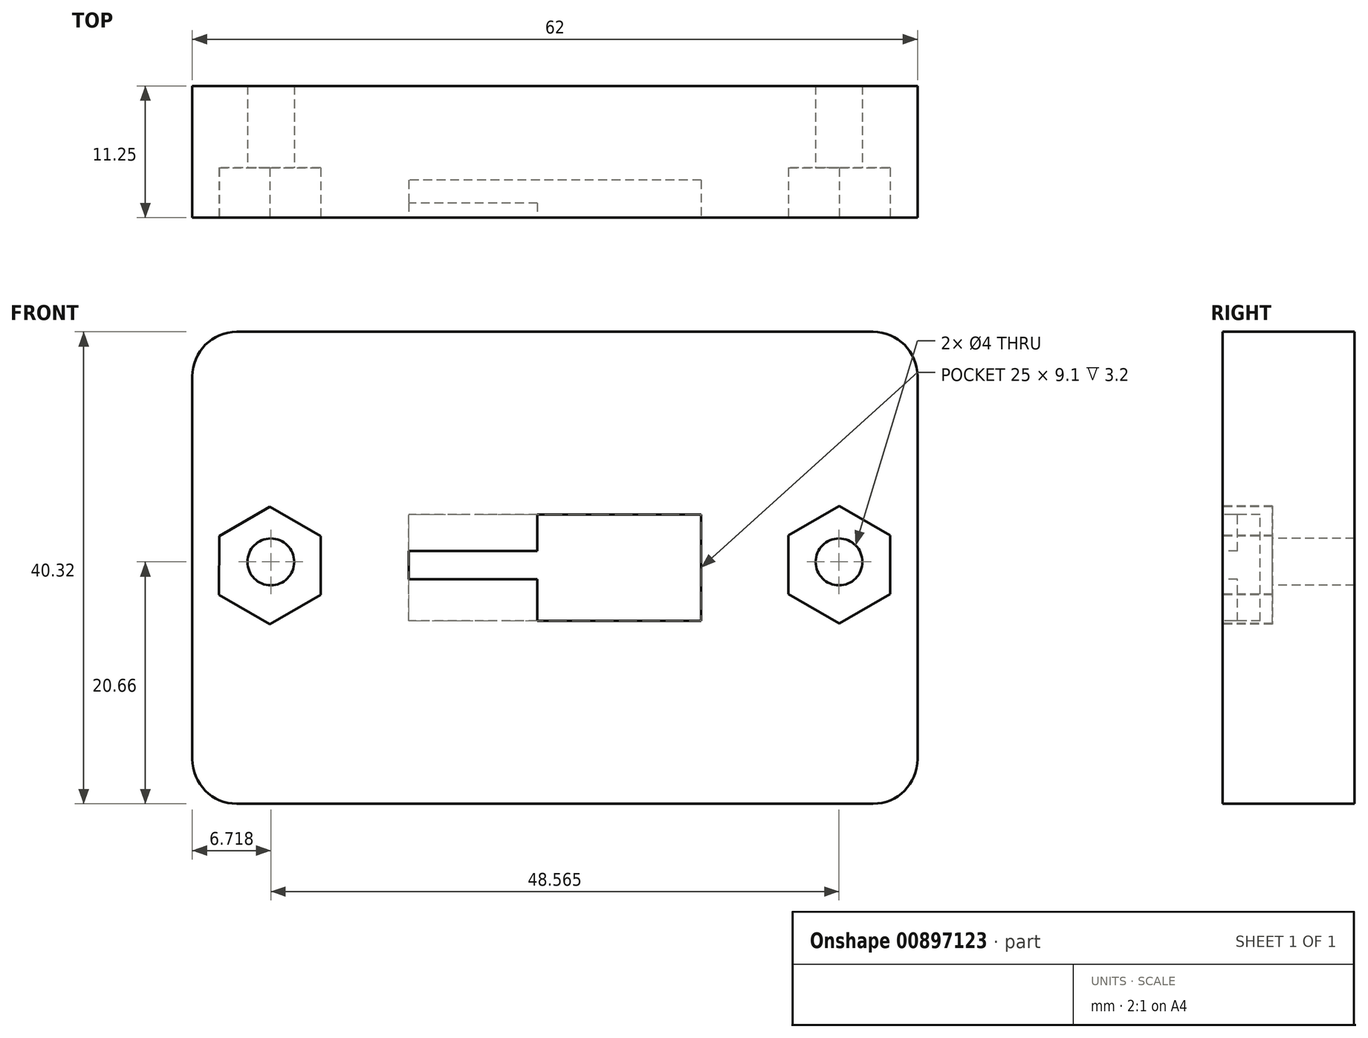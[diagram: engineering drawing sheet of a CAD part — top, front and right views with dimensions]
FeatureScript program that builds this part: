
annotation { "Feature Type Name" : "Feature", "Feature Type Description" : "" }
export const myFeature = defineFeature(function(context is Context, id is Id, definition is map)
    precondition{}
    {
        {
            var Q0;
            Q0=qCreatedBy(makeId("Front.planeOp"),FACE);
            var sketch = newSketch(context, id + "F0", { "sketchPlane" : qUnion([Q0])});
            skLineSegment(sketch, "E0.bottom", {"start": v(31, -20.16) * mm, "end": v(-31, -20.16) * mm});
            skLineSegment(sketch, "E0.top", {"start": v(31, 20.16) * mm, "end": v(-31, 20.16) * mm});
            skLineSegment(sketch, "E0.left", {"start": v(31, -20.16) * mm, "end": v(31, 20.16) * mm});
            skLineSegment(sketch, "E0.right", {"start": v(-31, -20.16) * mm, "end": v(-31, 20.16) * mm});
            skPoint(sketch, "E0.middle", {"position": v(0, 0) * mm});
            skSolve(sketch);
        }
        {
            var Q0;
            Q0=qSketchRegion(id+"F0",true);
            extrude(context, id + "F1", {"entities" : qUnion([Q0]), "depth" : 11.25 * mm, "offsetDistance" : 25.4 * mm});
        }
        {
            var Q0;
            Q0=makeQuery(id+"F1.opExtrude","CAP_FACE",FACE,{"disambiguationData":[OSD([sQuery(id+"F0.wireOp",EDGE,"E0.bottom"),sQuery(id+"F0.wireOp",EDGE,"E0.top"),sQuery(id+"F0.wireOp",EDGE,"E0.left"),sQuery(id+"F0.wireOp",EDGE,"E0.right")])],"isStart":false});
            var sketch = newSketch(context, id + "F2", { "sketchPlane" : qUnion([Q0])});
            skLineSegment(sketch, "E1.bottom", {"start": v(12.5, -4.55) * mm, "end": v(-12.5, -4.55) * mm});
            skLineSegment(sketch, "E1.top", {"start": v(12.5, 4.55) * mm, "end": v(-12.5, 4.55) * mm});
            skLineSegment(sketch, "E1.left", {"start": v(12.5, -4.55) * mm, "end": v(12.5, 4.55) * mm});
            skLineSegment(sketch, "E1.right", {"start": v(-12.5, -4.55) * mm, "end": v(-12.5, 4.55) * mm});
            skPoint(sketch, "E1.middle", {"position": v(0, 0) * mm});
            skSolve(sketch);
        }
        {
            var Q0;
            Q0=qSketchRegion(id+"F2",true);
            extrude(context, id + "F3", {"entities" : qUnion([Q0]), "operationType" : NewBodyOperationType.REMOVE, "oppositeDirection" : true, "depth" : 3.2 * mm, "offsetDistance" : 25.4 * mm});
        }
        {
            var Q0;
            Q0=makeQuery(id+"F1.opExtrude","CAP_FACE",FACE,{"disambiguationData":[OSD([sQuery(id+"F0.wireOp",EDGE,"E0.bottom"),sQuery(id+"F0.wireOp",EDGE,"E0.top"),sQuery(id+"F0.wireOp",EDGE,"E0.left"),sQuery(id+"F0.wireOp",EDGE,"E0.right")])],"isStart":false});
            var sketch = newSketch(context, id + "F4", { "sketchPlane" : qUnion([Q0])});
            skLineSegment(sketch, "E2.bottom", {"start": v(-12.5, 4.55) * mm, "end": v(-1.5, 4.55) * mm});
            skLineSegment(sketch, "E2.top", {"start": v(-12.5, 1.44) * mm, "end": v(-1.5, 1.44) * mm});
            skLineSegment(sketch, "E2.left", {"start": v(-12.5, 4.55) * mm, "end": v(-12.5, 1.44) * mm});
            skLineSegment(sketch, "E2.right", {"start": v(-1.5, 4.55) * mm, "end": v(-1.5, 1.44) * mm});
            skLineSegment(sketch, "E3.bottom", {"start": v(-12.5, -0.96) * mm, "end": v(-1.5, -0.96) * mm});
            skLineSegment(sketch, "E3.top", {"start": v(-12.5, -4.55) * mm, "end": v(-1.5, -4.55) * mm});
            skLineSegment(sketch, "E3.left", {"start": v(-12.5, -0.96) * mm, "end": v(-12.5, -4.55) * mm});
            skLineSegment(sketch, "E3.right", {"start": v(-1.5, -0.96) * mm, "end": v(-1.5, -4.55) * mm});
            skLineSegment(sketch, "E4.left", {"start": v(-12.5, 1.44) * mm, "end": v(-12.5, -0.96) * mm});
            skLineSegment(sketch, "E4.right", {"start": v(-1.5, 1.44) * mm, "end": v(-1.5, -0.96) * mm});
            skSolve(sketch);
        }
        {
            var Q0;
            Q0=makeQuery(id+"F4.imprint","IMPRINT",FACE,{"disambiguationData":[TD([[makeQuery(id+"F4.imprint","IMPRINT",EDGE,{"derivedFrom":sQuery(id+"F4.wireOp",EDGE,"E2.bottom")}),1.0]])]});
            var Q1;
            Q1=makeQuery(id+"F4.imprint","IMPRINT",FACE,{"disambiguationData":[TD([[makeQuery(id+"F4.imprint","IMPRINT",EDGE,{"derivedFrom":sQuery(id+"F4.wireOp",EDGE,"E3.top")}),-1.0]])]});
            extrude(context, id + "F5", {"entities" : qUnion([Q0, Q1]), "operationType" : NewBodyOperationType.ADD, "oppositeDirection" : true, "depth" : 1.25 * mm, "offsetDistance" : 25.4 * mm});
        }
        {
            var Q0;
            Q0=makeQuery(id+"F1.opExtrude","SWEPT_EDGE",EDGE,{"disambiguationData":[OSD([sQuery(id+"F0.wireOp",EDGE,"E0.top"),sQuery(id+"F0.wireOp",EDGE,"E0.right")])]});
            var Q1;
            Q1=makeQuery(id+"F1.opExtrude","SWEPT_EDGE",EDGE,{"disambiguationData":[OSD([sQuery(id+"F0.wireOp",EDGE,"E0.top"),sQuery(id+"F0.wireOp",EDGE,"E0.left")])]});
            var Q2;
            Q2=makeQuery(id+"F1.opExtrude","SWEPT_EDGE",EDGE,{"disambiguationData":[OSD([sQuery(id+"F0.wireOp",EDGE,"E0.bottom"),sQuery(id+"F0.wireOp",EDGE,"E0.left")])]});
            var Q3;
            Q3=makeQuery(id+"F1.opExtrude","SWEPT_EDGE",EDGE,{"disambiguationData":[OSD([sQuery(id+"F0.wireOp",EDGE,"E0.bottom"),sQuery(id+"F0.wireOp",EDGE,"E0.right")])]});
            fillet(context, id + "F6", {"entities" : qUnion([Q0, Q1, Q2, Q3]), "radius" : 3.8 * mm, "tangentPropagation" : true, "allowEdgeOverflow" : false});
        }
        {
            var Q0;
            Q0=makeQuery(id+"F5.boolean.opBoolean","MERGE",FACE,{"derivedFrom":[makeQuery(id+"F1.opExtrude","CAP_FACE",FACE,{"disambiguationData":[OSD([sQuery(id+"F0.wireOp",EDGE,"E0.bottom"),sQuery(id+"F0.wireOp",EDGE,"E0.top"),sQuery(id+"F0.wireOp",EDGE,"E0.left"),sQuery(id+"F0.wireOp",EDGE,"E0.right")])],"isStart":false}),makeQuery(id+"F5.opExtrude","CAP_FACE",FACE,{"disambiguationData":[OSD([sQuery(id+"F4.wireOp",EDGE,"E2.bottom"),sQuery(id+"F4.wireOp",EDGE,"E2.left"),sQuery(id+"F4.wireOp",EDGE,"E2.right"),sQuery(id+"F4.wireOp",EDGE,"E2.top")])],"isStart":true}),makeQuery(id+"F5.opExtrude","CAP_FACE",FACE,{"disambiguationData":[OSD([sQuery(id+"F4.wireOp",EDGE,"E3.top"),sQuery(id+"F4.wireOp",EDGE,"E3.left"),sQuery(id+"F4.wireOp",EDGE,"E3.right"),sQuery(id+"F4.wireOp",EDGE,"E3.bottom")])],"isStart":true})]});
            var sketch = newSketch(context, id + "F7", { "sketchPlane" : qUnion([Q0])});
            skLineSegment(sketch, "E5.left", {"start": v(24.28, 0) * mm, "end": v(24.28, 0) * mm});
            skLineSegment(sketch, "E5.right", {"start": v(-24.28, 0) * mm, "end": v(-24.28, 0) * mm});
            skPoint(sketch, "E5.middle", {"position": v(0, 0) * mm});
            skCircle(sketch, "E6", {"center": v(-24.28, 0.5) * mm, "radius": 2 * mm});
            skCircle(sketch, "E7", {"center": v(24.28, 0.5) * mm, "radius": 2 * mm});
            skSolve(sketch);
        }
        {
            var Q0;
            Q0=makeQuery(id+"F7.imprint","IMPRINT",FACE,{"disambiguationData":[TD([[makeQuery(id+"F7.imprint","IMPRINT",EDGE,{"derivedFrom":sQuery(id+"F7.wireOp",EDGE,"E6")}),1.0]])]});
            var Q1;
            Q1=makeQuery(id+"F7.imprint","IMPRINT",FACE,{"disambiguationData":[TD([[makeQuery(id+"F7.imprint","IMPRINT",EDGE,{"derivedFrom":sQuery(id+"F7.wireOp",EDGE,"E7")}),1.0]])]});
            var Q2;
            Q2=sQuery(id+"F7.wireOp",EDGE,"E6");
            var Q3;
            Q3=sQuery(id+"F7.wireOp",EDGE,"E7");
            extrude(context, id + "F8", {"entities" : qUnion([Q0, Q1]), "operationType" : NewBodyOperationType.REMOVE, "surfaceEntities" : qUnion([Q2, Q3]), "oppositeDirection" : true, "depth" : 15.24 * mm, "offsetDistance" : 25.4 * mm});
        }
        {
            var Q0;
            Q0=makeQuery(id+"F5.boolean.opBoolean","MERGE",FACE,{"derivedFrom":[makeQuery(id+"F1.opExtrude","CAP_FACE",FACE,{"disambiguationData":[OSD([sQuery(id+"F0.wireOp",EDGE,"E0.bottom"),sQuery(id+"F0.wireOp",EDGE,"E0.top"),sQuery(id+"F0.wireOp",EDGE,"E0.left"),sQuery(id+"F0.wireOp",EDGE,"E0.right")])],"isStart":false}),makeQuery(id+"F5.opExtrude","CAP_FACE",FACE,{"disambiguationData":[OSD([sQuery(id+"F4.wireOp",EDGE,"E2.bottom"),sQuery(id+"F4.wireOp",EDGE,"E2.left"),sQuery(id+"F4.wireOp",EDGE,"E2.right"),sQuery(id+"F4.wireOp",EDGE,"E2.top")])],"isStart":true}),makeQuery(id+"F5.opExtrude","CAP_FACE",FACE,{"disambiguationData":[OSD([sQuery(id+"F4.wireOp",EDGE,"E3.top"),sQuery(id+"F4.wireOp",EDGE,"E3.left"),sQuery(id+"F4.wireOp",EDGE,"E3.right"),sQuery(id+"F4.wireOp",EDGE,"E3.bottom")])],"isStart":true})]});
            var sketch = newSketch(context, id + "F9", { "sketchPlane" : qUnion([Q0])});
            skCircle(sketch, "E8.cCircle", {"center": v(-24.36, 0.2) * mm, "radius": 4.34 * mm, "construction": true});
            skLineSegment(sketch, "E8.0", {"start": v(-20.02, -2.31) * mm, "end": v(-24.37, -4.81) * mm});
            skLineSegment(sketch, "E8.1", {"start": v(-24.37, -4.81) * mm, "end": v(-28.7, -2.3) * mm});
            skLineSegment(sketch, "E8.2", {"start": v(-28.7, -2.3) * mm, "end": v(-28.7, 2.71) * mm});
            skLineSegment(sketch, "E8.3", {"start": v(-28.7, 2.71) * mm, "end": v(-24.36, 5.21) * mm});
            skLineSegment(sketch, "E8.4", {"start": v(-24.36, 5.21) * mm, "end": v(-20.02, 2.7) * mm});
            skLineSegment(sketch, "E8.5", {"start": v(-20.02, 2.7) * mm, "end": v(-20.02, -2.31) * mm});
            skPoint(sketch, "E8.0.midPoint", {"position": v(-22.2, -3.56) * mm});
            skCircle(sketch, "E9.cCircle", {"center": v(24.3, 0.26) * mm, "radius": 4.34 * mm, "construction": true});
            skLineSegment(sketch, "E9.0", {"start": v(28.65, -2.26) * mm, "end": v(24.3, -4.76) * mm});
            skLineSegment(sketch, "E9.1", {"start": v(24.3, -4.76) * mm, "end": v(19.96, -2.25) * mm});
            skLineSegment(sketch, "E9.2", {"start": v(19.96, -2.25) * mm, "end": v(19.97, 2.77) * mm});
            skLineSegment(sketch, "E9.3", {"start": v(19.97, 2.77) * mm, "end": v(24.31, 5.27) * mm});
            skLineSegment(sketch, "E9.4", {"start": v(24.31, 5.27) * mm, "end": v(28.65, 2.76) * mm});
            skLineSegment(sketch, "E9.5", {"start": v(28.65, 2.76) * mm, "end": v(28.65, -2.26) * mm});
            skPoint(sketch, "E9.0.midPoint", {"position": v(26.48, -3.5) * mm});
            skSolve(sketch);
        }
        {
            var Q0;
            Q0 = qSketchRegion(id + "F9", true);
            extrude(context, id + "F10", {"entities" : qUnion([Q0]), "operationType" : NewBodyOperationType.REMOVE, "oppositeDirection" : true, "depth" : 4.25 * mm, "offsetDistance" : 25.4 * mm});
        }
    });
